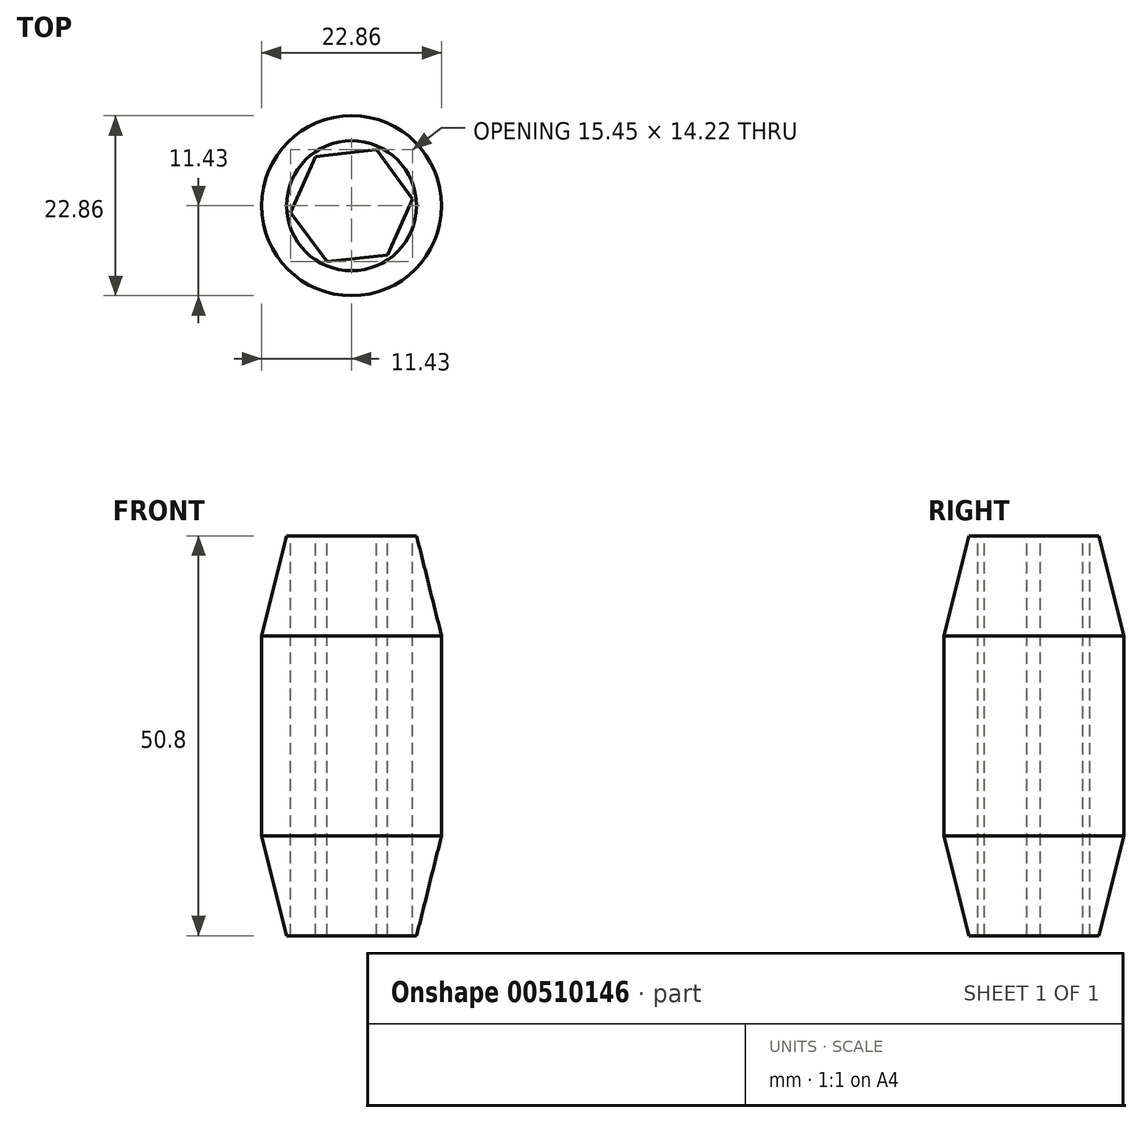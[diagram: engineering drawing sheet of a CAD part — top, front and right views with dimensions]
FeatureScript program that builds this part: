
annotation { "Feature Type Name" : "Feature", "Feature Type Description" : "" }
export const myFeature = defineFeature(function(context is Context, id is Id, definition is map)
    precondition{}
    {
        {
            var Q0;
            Q0=qCreatedBy(makeId("Top.planeOp"),FACE);
            var sketch = newSketch(context, id + "F0", { "sketchPlane" : qUnion([Q0])});
            skCircle(sketch, "E0.cCircle", {"center": v(0, 0) * mm, "radius": 6.73 * mm, "construction": true});
            skLineSegment(sketch, "E0.0", {"start": v(3.14, 7.11) * mm, "end": v(7.73, 0.84) * mm});
            skLineSegment(sketch, "E0.1", {"start": v(7.73, 0.84) * mm, "end": v(4.6, -6.27) * mm});
            skLineSegment(sketch, "E0.2", {"start": v(4.6, -6.27) * mm, "end": v(-3.14, -7.11) * mm});
            skLineSegment(sketch, "E0.3", {"start": v(-3.14, -7.11) * mm, "end": v(-7.73, -0.84) * mm});
            skLineSegment(sketch, "E0.4", {"start": v(-7.73, -0.84) * mm, "end": v(-4.6, 6.27) * mm});
            skLineSegment(sketch, "E0.5", {"start": v(-4.6, 6.27) * mm, "end": v(3.14, 7.11) * mm});
            skPoint(sketch, "E0.0.midPoint", {"position": v(5.43, 3.98) * mm});
            skSolve(sketch);
        }
        {
            var Q0;
            Q0=qCreatedBy(makeId("Right.planeOp"),FACE);
            var sketch = newSketch(context, id + "F1", { "sketchPlane" : qUnion([Q0])});
            skLineSegment(sketch, "E1", {"start": v(0, 42.33) * mm, "end": v(0, -42.42) * mm, "construction": true});
            skLineSegment(sketch, "E2", {"start": v(6.73, 24.94) * mm, "end": v(6.73, -25.86) * mm});
            skLineSegment(sketch, "E3", {"start": v(11.43, 12.24) * mm, "end": v(11.43, -13.16) * mm});
            skLineSegment(sketch, "E4", {"start": v(11.43, 12.24) * mm, "end": v(8.25, 24.94) * mm});
            skLineSegment(sketch, "E5", {"start": v(11.43, -13.16) * mm, "end": v(8.26, -25.86) * mm});
            skLineSegment(sketch, "E6", {"start": v(8.25, -25.86) * mm, "end": v(6.73, -25.86) * mm});
            skLineSegment(sketch, "E7", {"start": v(8.25, 24.94) * mm, "end": v(6.73, 24.94) * mm});
            skSolve(sketch);
        }
        {
            var Q0;
            Q0=qSketchRegion(id+"F1",true);
            var Q1;
            Q1=sQuery(id+"F1.wireOp",EDGE,"E1");
            revolve(context, id + "F2", {"entities" : qUnion([Q0]), "axis" : qUnion([Q1]), "revolveType" : RevolveType.FULL});
        }
        {
            var Q0;
            Q0=qSketchRegion(id+"F0",true);
            extrude(context, id + "F3", {"entities" : qUnion([Q0]), "operationType" : NewBodyOperationType.REMOVE, "oppositeDirection" : true, "depth" : 38.1 * mm, "hasSecondDirection" : true, "secondDirectionOppositeDirection" : false, "secondDirectionDepth" : 38.1 * mm});
        }
    });
